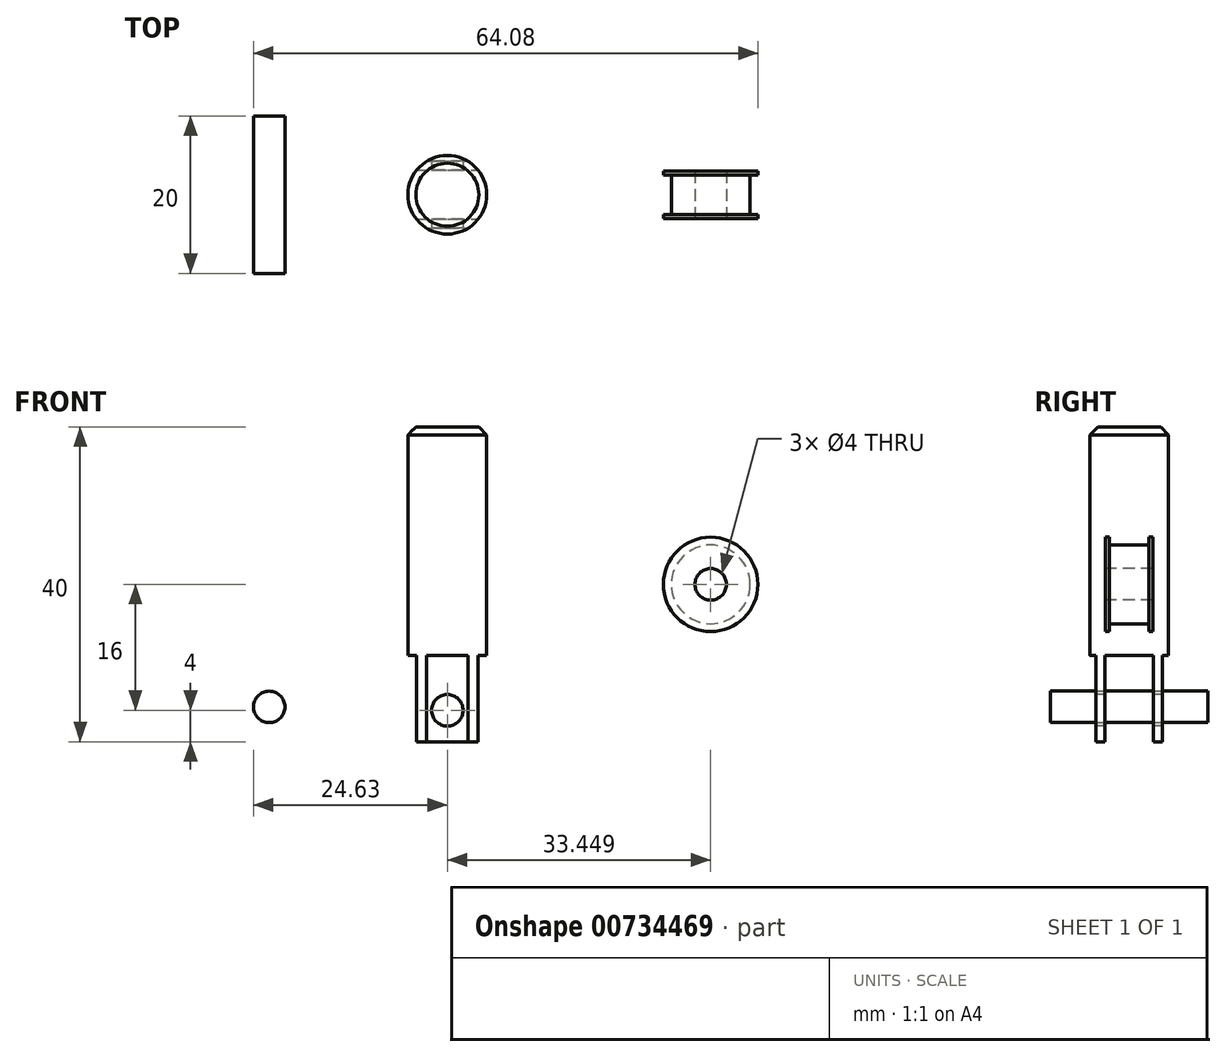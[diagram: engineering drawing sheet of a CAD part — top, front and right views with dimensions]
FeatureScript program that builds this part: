
annotation { "Feature Type Name" : "Feature", "Feature Type Description" : "" }
export const myFeature = defineFeature(function(context is Context, id is Id, definition is map)
    precondition{}
    {
        {
            var Q0;
            Q0=qCreatedBy(makeId("Front.planeOp"),FACE);
            var sketch = newSketch(context, id + "F0", { "sketchPlane" : qUnion([Q0])});
            skLineSegment(sketch, "E0", {"start": v(0, 20) * mm, "end": v(-5, 20) * mm});
            skLineSegment(sketch, "E1", {"start": v(-5, 20) * mm, "end": v(-5, -20) * mm});
            skLineSegment(sketch, "E2", {"start": v(-5, -20) * mm, "end": v(0, -20) * mm});
            skLineSegment(sketch, "E3", {"start": v(0, -20) * mm, "end": v(0, 20) * mm});
            skSolve(sketch);
        }
        {
            var Q0;
            Q0 = qSketchRegion(id + "F0", true);
            var Q1;
            Q1=sQuery(id+"F0.wireOp",EDGE,"E3");
            revolve(context, id + "F1", {"surfaceOperationType" : NewSurfaceOperationType.NEW, "entities" : qUnion([Q0]), "axis" : qUnion([Q1]), "revolveType" : RevolveType.FULL});
        }
        {
            var Q0;
            Q0=makeQuery(id+"F1.opRevolve","SWEPT_FACE",FACE,{"disambiguationData":[OSD([sQuery(id+"F0.wireOp",EDGE,"E2")])]});
            var sketch = newSketch(context, id + "F2", { "sketchPlane" : qUnion([Q0])});
            skLineSegment(sketch, "E4.bottom", {"start": v(-9, 3.1) * mm, "end": v(9, 3.1) * mm});
            skLineSegment(sketch, "E4.top", {"start": v(-9, -3.1) * mm, "end": v(9, -3.1) * mm});
            skLineSegment(sketch, "E4.left", {"start": v(-9, 3.1) * mm, "end": v(-9, -3.1) * mm});
            skLineSegment(sketch, "E4.right", {"start": v(9, 3.1) * mm, "end": v(9, -3.1) * mm});
            skLineSegment(sketch, "E5.bottom", {"start": v(-4.48, -6.54) * mm, "end": v(4.48, -6.54) * mm});
            skLineSegment(sketch, "E5.top", {"start": v(-4.48, -4.25) * mm, "end": v(4.48, -4.25) * mm});
            skLineSegment(sketch, "E5.left", {"start": v(-4.48, -6.54) * mm, "end": v(-4.48, -4.25) * mm});
            skLineSegment(sketch, "E5.right", {"start": v(4.48, -6.54) * mm, "end": v(4.48, -4.25) * mm});
            skLineSegment(sketch, "E6", {"start": v(-15.14, -5) * mm, "end": v(12.93, -5) * mm, "construction": true});
            skLineSegment(sketch, "E7.MirrorCS", {"start": v(-4.48, 4.25) * mm, "end": v(4.48, 4.25) * mm});
            skLineSegment(sketch, "E8.MirrorCS", {"start": v(4.48, 6.54) * mm, "end": v(4.48, 4.25) * mm});
            skLineSegment(sketch, "E9.MirrorCS", {"start": v(-4.48, 6.54) * mm, "end": v(4.48, 6.54) * mm});
            skLineSegment(sketch, "E10.MirrorCS", {"start": v(-4.48, 6.54) * mm, "end": v(-4.48, 4.25) * mm});
            skPoint(sketch, "E11", {"position": v(-2.63, 4.25) * mm});
            skPoint(sketch, "E12", {"position": v(2.63, 4.25) * mm});
            skSolve(sketch);
        }
        {
            var Q0;
            Q0 = qSketchRegion(id + "F2", true);
            extrude(context, id + "F3", {"entities" : qUnion([Q0]), "operationType" : NewBodyOperationType.REMOVE, "oppositeDirection" : true, "depth" : 11 * mm, "offsetDistance" : 25 * mm});
        }
        {
            var Q0;
            Q0=makeQuery(id+"F3.boolean.opBoolean","COPY",FACE,{"derivedFrom":makeQuery(id+"F3.opExtrude","SWEPT_FACE",FACE,{"disambiguationData":[OSD([sQuery(id+"F2.wireOp",EDGE,"E4.top")])]})});
            var sketch = newSketch(context, id + "F4", { "sketchPlane" : qUnion([Q0])});
            skCircle(sketch, "E13", {"center": v(0, -16) * mm, "radius": 2 * mm});
            skSolve(sketch);
        }
        {
            var Q0;
            Q0 = qSketchRegion(id + "F4", true);
            extrude(context, id + "F5", {"entities" : qUnion([Q0]), "operationType" : NewBodyOperationType.REMOVE, "oppositeDirection" : true, "depth" : 25 * mm, "offsetDistance" : 25 * mm, "symmetric" : true});
        }
        {
            var Q0;
            Q0=qCreatedBy(makeId("Front.planeOp"),FACE);
            var sketch = newSketch(context, id + "F6", { "sketchPlane" : qUnion([Q0])});
            skCircle(sketch, "E14", {"center": v(-22.63, -15.56) * mm, "radius": 2 * mm});
            skSolve(sketch);
        }
        {
            var Q0;
            Q0 = qSketchRegion(id + "F6", true);
            extrude(context, id + "F7", {"entities" : qUnion([Q0]), "depth" : 20 * mm, "offsetDistance" : 25 * mm, "symmetric" : true});
        }
        {
            var Q0;
            Q0=qCreatedBy(makeId("Top.planeOp"),FACE);
            var sketch = newSketch(context, id + "F8", { "sketchPlane" : qUnion([Q0])});
            skLineSegment(sketch, "E15", {"start": v(33.45, -19.62) * mm, "end": v(33.45, 17.6) * mm, "construction": true});
            skLineSegment(sketch, "E16", {"start": v(31.45, -7.68) * mm, "end": v(31.45, 7.1) * mm, "construction": true});
            skLineSegment(sketch, "E17", {"start": v(25.83, -3) * mm, "end": v(38.2, -3) * mm, "construction": true});
            skLineSegment(sketch, "E18", {"start": v(25.8, 3) * mm, "end": v(38.87, 3) * mm, "construction": true});
            skLineSegment(sketch, "E19", {"start": v(27.45, -5.85) * mm, "end": v(27.45, 6.16) * mm, "construction": true});
            skLineSegment(sketch, "E20", {"start": v(31.45, -3) * mm, "end": v(27.45, -3) * mm});
            skLineSegment(sketch, "E21", {"start": v(27.45, 3) * mm, "end": v(31.45, 3) * mm});
            skLineSegment(sketch, "E22", {"start": v(31.45, 3) * mm, "end": v(31.45, -3) * mm});
            skLineSegment(sketch, "E23", {"start": v(25.85, -2.5) * mm, "end": v(38.18, -2.5) * mm, "construction": true});
            skLineSegment(sketch, "E24", {"start": v(28.45, 6.14) * mm, "end": v(28.45, -5.76) * mm, "construction": true});
            skLineSegment(sketch, "E25.MirrorCS", {"start": v(25.85, 2.5) * mm, "end": v(38.18, 2.5) * mm, "construction": true});
            skLineSegment(sketch, "E26", {"start": v(27.45, 3) * mm, "end": v(27.45, 2.5) * mm});
            skLineSegment(sketch, "E27", {"start": v(27.45, 2.5) * mm, "end": v(28.45, 2.5) * mm});
            skLineSegment(sketch, "E28", {"start": v(28.45, 2.5) * mm, "end": v(28.45, -2.5) * mm});
            skLineSegment(sketch, "E29", {"start": v(28.45, -2.5) * mm, "end": v(27.45, -2.5) * mm});
            skLineSegment(sketch, "E30", {"start": v(27.45, -2.5) * mm, "end": v(27.45, -3) * mm});
            skSolve(sketch);
        }
        {
            var Q0;
            Q0 = qSketchRegion(id + "F8", true);
            var Q1;
            Q1=sQuery(id+"F8.wireOp",EDGE,"E15");
            revolve(context, id + "F9", {"surfaceOperationType" : NewSurfaceOperationType.NEW, "entities" : qUnion([Q0]), "axis" : qUnion([Q1]), "revolveType" : RevolveType.FULL});
        }
        {
            var Q0;
            Q0=makeQuery(id+"F1.opRevolve","SWEPT_EDGE",EDGE,{"disambiguationData":[OSD([sQuery(id+"F0.wireOp",EDGE,"E0"),sQuery(id+"F0.wireOp",EDGE,"E1")])]});
            chamfer(context, id + "F10", {"entities" : qUnion([Q0]), "width" : 1 * mm, "tangentPropagation" : true});
        }
        {
            var Q0;
            Q0 = qSketchRegion(id + "F2", true);
            extrude(context, id + "F11", {"entities" : qUnion([Q0]), "operationType" : NewBodyOperationType.REMOVE, "oppositeDirection" : true, "depth" : 10 * mm, "offsetDistance" : 25 * mm});
        }
    });
